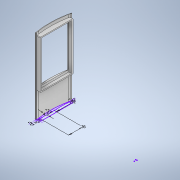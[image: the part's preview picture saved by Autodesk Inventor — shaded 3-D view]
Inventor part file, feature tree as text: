
AUTODESK INVENTOR PART (.ipt)
format: ipt  version: 2022 (Build 260153000, 153)  size: 227,328 bytes
history: native  units: mm
features: extrude x8, fillet x2, sketch x1
ambient origin geometry x8: Origin, YZ Plane, XZ Plane, XY Plane, X Axis, Y Axis, Z Axis, Center Point
bodies: Solid1 (feature_tree)
feature tree (11):
  sketch  "Sketch1"  dims[d15=4.5mm d17=2.0mm d18=2.0mm d19=2.0mm d20=2.0mm d21=2.0mm d22=32.0mm d24=26.0mm d33=138.0mm d34=0.0mm d86=133.0mm d87=0.0mm d88=131.0mm d89=0.0mm d90=129.0mm d91=0.0mm d92=129.0mm d93=0.0mm d94=51.0mm d95=0.0mm d96=47.0mm d97=0.0mm d102=45.0mm d103=0.0mm d104=2.0mm d105=1.0mm d35=0.5mm d36=0.872665mm d59=0.0mm d60=0.0mm d61=0.0mm d62=0.0mm d68=0.5mm d69=0.872665mm d70=0.5mm d71=0.872665mm d84=0.5mm d85=0.872665mm d106=0.5mm d107=0.872665mm]
  extrude  "Extrusion1"  Depth=1.0mm
  extrude  "Extrusion24"  Depth=1.0mm
  extrude  "Extrusion25"  Depth=1.0mm
  extrude  "Extrusion26"  Depth=1.0mm
  extrude  "Extrusion27"  Depth=1.0mm
  extrude  "Extrusion28"  Depth=1.0mm
  extrude  "Extrusion29"  Depth=1.0mm
  extrude  "Extrusion32"  Depth=1.0mm TaperAngle=0.0deg
  fillet  "Fillet4"  Radius=133.0mm
  fillet  "Fillet5"  Radius=131.0mm
